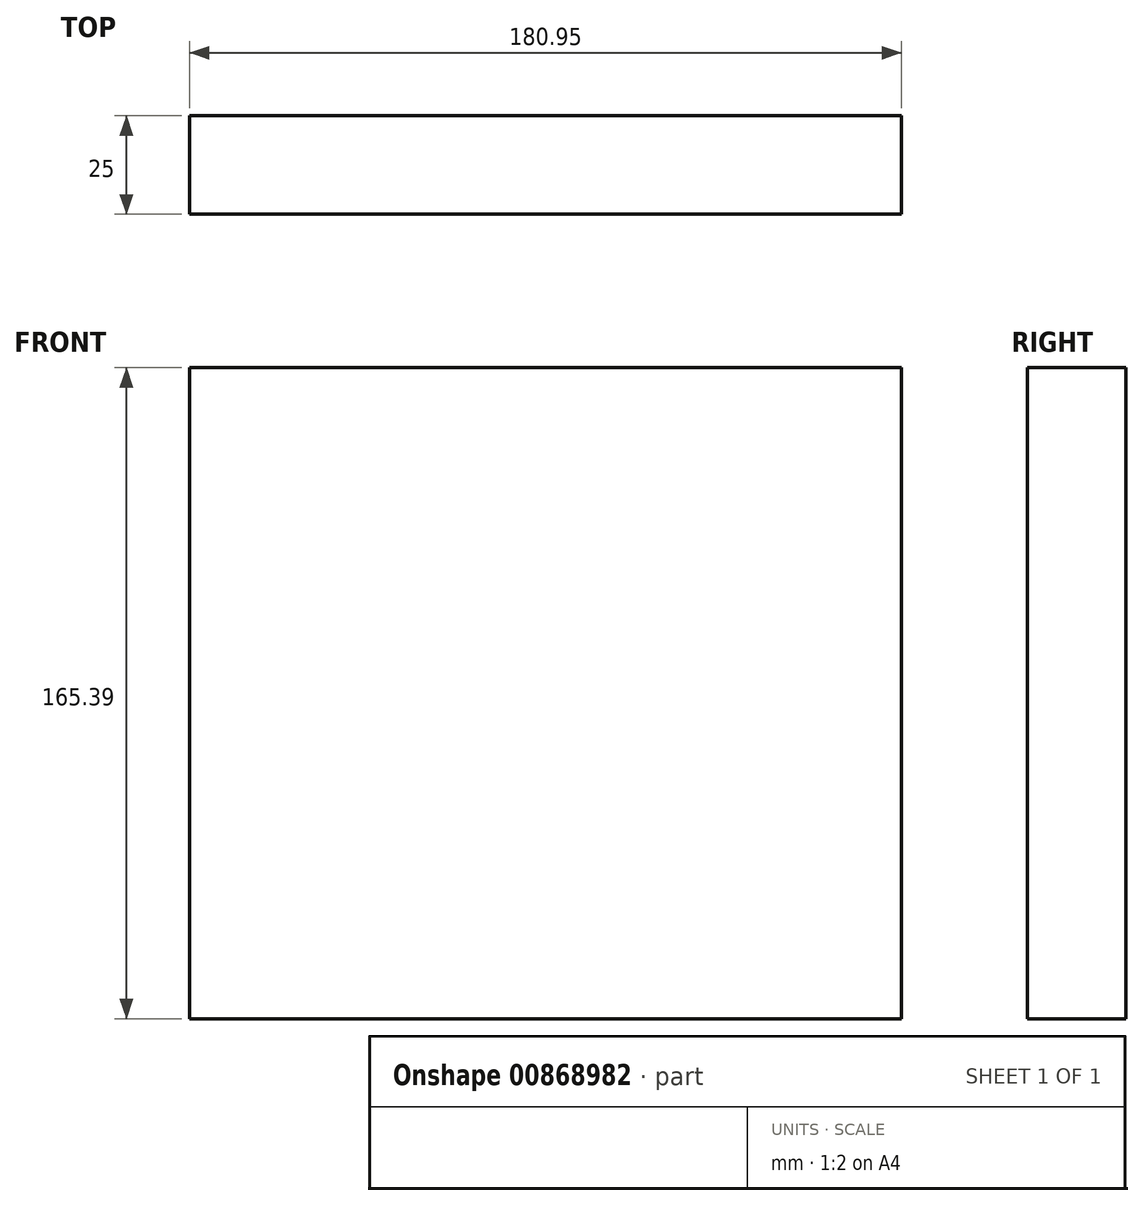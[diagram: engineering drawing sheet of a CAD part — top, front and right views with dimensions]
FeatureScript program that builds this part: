
annotation { "Feature Type Name" : "Feature", "Feature Type Description" : "" }
export const myFeature = defineFeature(function(context is Context, id is Id, definition is map)
    precondition{}
    {
        {
            var Q0;
            Q0=qCreatedBy(makeId("Front.planeOp"),FACE);
            var sketch = newSketch(context, id + "F0", { "sketchPlane" : qUnion([Q0])});
            skLineSegment(sketch, "E0.bottom", {"start": v(0, 0) * mm, "end": v(180.95, 0) * mm});
            skLineSegment(sketch, "E0.top", {"start": v(0, -165.39) * mm, "end": v(180.95, -165.39) * mm});
            skLineSegment(sketch, "E0.left", {"start": v(0, 0) * mm, "end": v(0, -165.39) * mm});
            skLineSegment(sketch, "E0.right", {"start": v(180.95, 0) * mm, "end": v(180.95, -165.39) * mm});
            skSolve(sketch);
        }
        {
            var Q0;
            Q0 = qSketchRegion(id + "F0", true);
            extrude(context, id + "F1", {"entities" : qUnion([Q0]), "depth" : 25 * mm, "offsetDistance" : 25 * mm});
        }
    });
